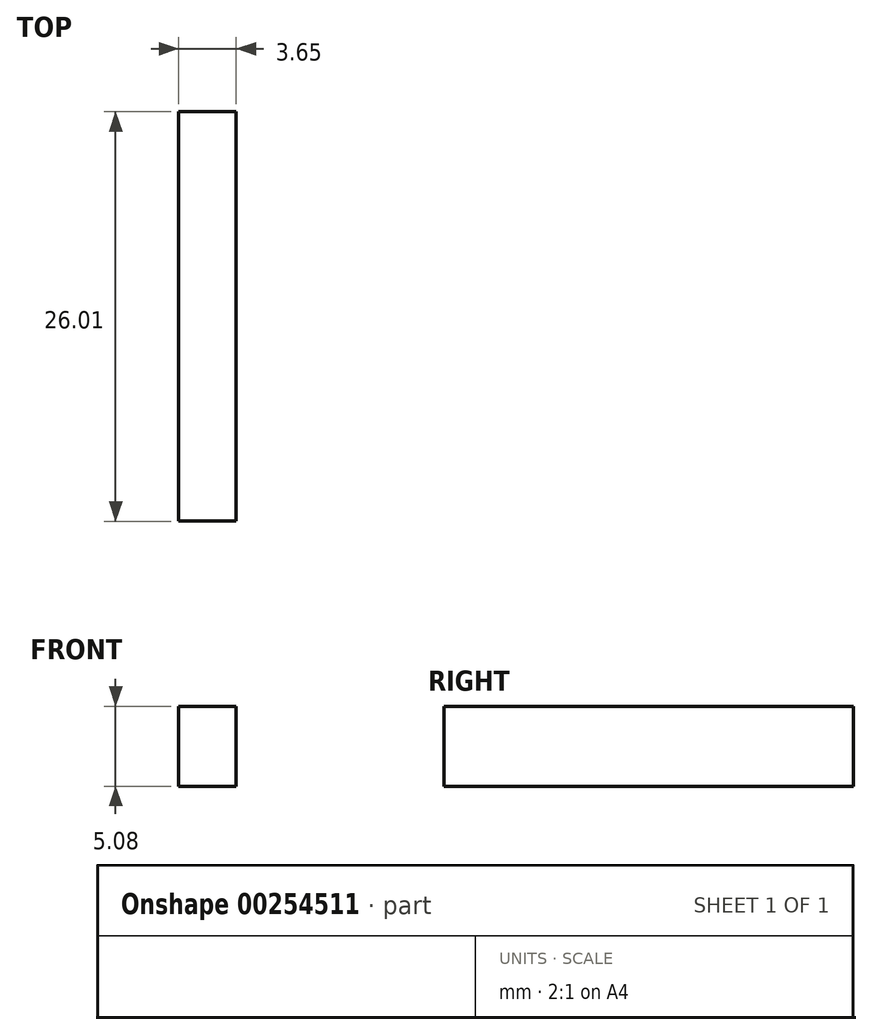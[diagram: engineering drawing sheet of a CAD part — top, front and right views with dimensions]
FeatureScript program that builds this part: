
annotation { "Feature Type Name" : "Feature", "Feature Type Description" : "" }
export const myFeature = defineFeature(function(context is Context, id is Id, definition is map)
    precondition{}
    {
        {
            var Q0;
            Q0=qCreatedBy(makeId("Top.planeOp"),FACE);
            var sketch = newSketch(context, id + "F0", { "sketchPlane" : qUnion([Q0])});
            skLineSegment(sketch, "E0", {"start": v(-33.45, 9.2) * mm, "end": v(-26.8, 16.12) * mm});
            skLineSegment(sketch, "E1", {"start": v(-26.8, 16.12) * mm, "end": v(-22.17, 16.12) * mm});
            skLineSegment(sketch, "E2", {"start": v(-22.17, 16.12) * mm, "end": v(-22.17, 19.99) * mm});
            skLineSegment(sketch, "E3", {"start": v(-22.17, 19.99) * mm, "end": v(-25.8, 19.97) * mm});
            skLineSegment(sketch, "E4", {"start": v(-25.8, 19.97) * mm, "end": v(-25.8, 38.73) * mm});
            skLineSegment(sketch, "E5", {"start": v(-25.8, 38.73) * mm, "end": v(-18.88, 45.9) * mm});
            skLineSegment(sketch, "E6", {"start": v(-18.88, 45.9) * mm, "end": v(14.3, 45.9) * mm});
            skLineSegment(sketch, "E7", {"start": v(14.3, 45.9) * mm, "end": v(22.2, 38.73) * mm});
            skLineSegment(sketch, "E8", {"start": v(22.2, 38.73) * mm, "end": v(22.2, 19.97) * mm});
            skLineSegment(sketch, "E9", {"start": v(22.2, 19.97) * mm, "end": v(18.52, 19.97) * mm});
            skLineSegment(sketch, "E10", {"start": v(18.52, 19.97) * mm, "end": v(18.52, 16.12) * mm});
            skLineSegment(sketch, "E11", {"start": v(18.52, 16.12) * mm, "end": v(22.2, 16.12) * mm});
            skLineSegment(sketch, "E12", {"start": v(22.2, 16.12) * mm, "end": v(29.83, 9.43) * mm});
            skLineSegment(sketch, "E13", {"start": v(29.83, 9.43) * mm, "end": v(29.83, -20.85) * mm});
            skLineSegment(sketch, "E14", {"start": v(29.83, -20.85) * mm, "end": v(22.14, -20.85) * mm});
            skLineSegment(sketch, "E15", {"start": v(22.14, -20.85) * mm, "end": v(22.14, -32.04) * mm});
            skLineSegment(sketch, "E16", {"start": v(22.14, -32.04) * mm, "end": v(19.03, -35.7) * mm});
            skLineSegment(sketch, "E17", {"start": v(19.03, -35.7) * mm, "end": v(3.87, -35.7) * mm});
            skLineSegment(sketch, "E18", {"start": v(3.87, -35.7) * mm, "end": v(3.87, -28.47) * mm});
            skLineSegment(sketch, "E19", {"start": v(3.87, -28.47) * mm, "end": v(-7.29, -28.47) * mm});
            skLineSegment(sketch, "E20", {"start": v(-7.29, -28.47) * mm, "end": v(-7.29, -35.7) * mm});
            skLineSegment(sketch, "E21", {"start": v(-7.29, -35.7) * mm, "end": v(-23.05, -35.7) * mm});
            skLineSegment(sketch, "E22", {"start": v(-23.05, -35.7) * mm, "end": v(-25.8, -32.44) * mm});
            skLineSegment(sketch, "E23", {"start": v(-25.8, -32.44) * mm, "end": v(-25.8, -20.85) * mm});
            skLineSegment(sketch, "E24", {"start": v(-25.8, -20.85) * mm, "end": v(-33.32, -20.85) * mm});
            skLineSegment(sketch, "E25", {"start": v(-33.32, -20.85) * mm, "end": v(-33.45, 9.2) * mm});
            skCircle(sketch, "E26", {"center": v(-11.3, 31.23) * mm, "radius": 5.9 * mm});
            skPoint(sketch, "E26.first.point", {"position": v(-17.19, 30.94) * mm});
            skPoint(sketch, "E26.second.point", {"position": v(-5.4, 31.07) * mm});
            skPoint(sketch, "E26.third.point", {"position": v(-11.26, 25.33) * mm});
            skCircle(sketch, "E27", {"center": v(7.12, 31) * mm, "radius": 5.64 * mm});
            skPoint(sketch, "E27.first.point", {"position": v(1.48, 30.84) * mm});
            skPoint(sketch, "E27.second.point", {"position": v(12.76, 30.78) * mm});
            skPoint(sketch, "E27.third.point", {"position": v(7.1, 36.64) * mm});
            skLineSegment(sketch, "E28.bottom", {"start": v(-14.96, 34.57) * mm, "end": v(-7.5, 34.57) * mm});
            skLineSegment(sketch, "E28.top", {"start": v(-14.96, 27.44) * mm, "end": v(-7.5, 27.44) * mm});
            skLineSegment(sketch, "E28.left", {"start": v(-14.96, 34.57) * mm, "end": v(-14.96, 27.44) * mm});
            skLineSegment(sketch, "E28.right", {"start": v(-7.5, 34.57) * mm, "end": v(-7.5, 27.44) * mm});
            skLineSegment(sketch, "E29.bottom", {"start": v(3.8, 34.28) * mm, "end": v(10.72, 34.28) * mm});
            skLineSegment(sketch, "E29.top", {"start": v(3.8, 27.44) * mm, "end": v(10.72, 27.44) * mm});
            skLineSegment(sketch, "E29.left", {"start": v(3.8, 34.28) * mm, "end": v(3.8, 27.44) * mm});
            skLineSegment(sketch, "E29.right", {"start": v(10.72, 34.28) * mm, "end": v(10.72, 27.44) * mm});
            skLineSegment(sketch, "E30.bottom", {"start": v(7.12, 31) * mm, "end": v(3.8, 31) * mm});
            skLineSegment(sketch, "E30.top", {"start": v(7.12, 34.28) * mm, "end": v(3.8, 34.28) * mm});
            skLineSegment(sketch, "E30.left", {"start": v(7.12, 31) * mm, "end": v(7.12, 34.28) * mm});
            skLineSegment(sketch, "E30.right", {"start": v(3.8, 31) * mm, "end": v(3.8, 34.28) * mm});
            skLineSegment(sketch, "E31.bottom", {"start": v(-11.3, 31.23) * mm, "end": v(-14.96, 31.23) * mm});
            skLineSegment(sketch, "E31.top", {"start": v(-11.3, 34.57) * mm, "end": v(-14.96, 34.57) * mm});
            skLineSegment(sketch, "E31.left", {"start": v(-11.3, 31.23) * mm, "end": v(-11.3, 34.57) * mm});
            skLineSegment(sketch, "E31.right", {"start": v(-14.96, 31.23) * mm, "end": v(-14.96, 34.57) * mm});
            skLineSegment(sketch, "E32.bottom", {"start": v(-3.8, 23.6) * mm, "end": v(0, 23.6) * mm});
            skLineSegment(sketch, "E32.top", {"start": v(-3.8, 19.8) * mm, "end": v(0, 19.8) * mm});
            skLineSegment(sketch, "E32.left", {"start": v(-3.8, 23.6) * mm, "end": v(-3.8, 19.8) * mm});
            skLineSegment(sketch, "E32.right", {"start": v(0, 23.6) * mm, "end": v(0, 19.8) * mm});
            skLineSegment(sketch, "E33.bottom", {"start": v(-7.5, 15.86) * mm, "end": v(3.8, 15.86) * mm});
            skLineSegment(sketch, "E33.top", {"start": v(-7.5, 12.27) * mm, "end": v(3.8, 12.27) * mm});
            skLineSegment(sketch, "E33.left", {"start": v(-7.5, 15.86) * mm, "end": v(-7.5, 12.27) * mm});
            skLineSegment(sketch, "E33.right", {"start": v(3.8, 15.86) * mm, "end": v(3.8, 12.27) * mm});
            skPoint(sketch, "E34.oppositeSnap0", {"position": v(-25.8, -26.64) * mm});
            skLineSegment(sketch, "E34.bottom", {"start": v(-29.45, -9.9) * mm, "end": v(-25.8, -9.9) * mm});
            skLineSegment(sketch, "E34.top", {"start": v(-29.45, -17.27) * mm, "end": v(-25.8, -17.27) * mm});
            skLineSegment(sketch, "E34.left", {"start": v(-29.45, -9.9) * mm, "end": v(-29.45, -17.27) * mm});
            skLineSegment(sketch, "E34.right", {"start": v(-25.8, -9.9) * mm, "end": v(-25.8, -17.27) * mm});
            skLineSegment(sketch, "E35.top", {"start": v(-29.45, 8.74) * mm, "end": v(-25.8, 8.74) * mm});
            skLineSegment(sketch, "E35.left", {"start": v(-29.45, -9.9) * mm, "end": v(-29.45, 8.74) * mm});
            skLineSegment(sketch, "E35.right", {"start": v(-25.8, -9.9) * mm, "end": v(-25.8, 8.74) * mm});
            skLineSegment(sketch, "E36.bottom", {"start": v(22.2, -9.9) * mm, "end": v(25.76, -9.9) * mm});
            skLineSegment(sketch, "E36.top", {"start": v(22.2, -17.27) * mm, "end": v(25.76, -17.27) * mm});
            skLineSegment(sketch, "E36.left", {"start": v(22.2, -9.9) * mm, "end": v(22.2, -17.27) * mm});
            skLineSegment(sketch, "E36.right", {"start": v(25.76, -9.9) * mm, "end": v(25.76, -17.27) * mm});
            skLineSegment(sketch, "E37.top", {"start": v(22.2, 8.7) * mm, "end": v(25.76, 8.7) * mm});
            skLineSegment(sketch, "E37.left", {"start": v(22.2, -9.9) * mm, "end": v(22.2, 8.7) * mm});
            skLineSegment(sketch, "E37.right", {"start": v(25.76, -9.9) * mm, "end": v(25.76, 8.7) * mm});
            skLineSegment(sketch, "E38.bottom", {"start": v(-3.6, -28.47) * mm, "end": v(0, -28.47) * mm});
            skLineSegment(sketch, "E38.top", {"start": v(-3.6, -24.74) * mm, "end": v(0, -24.74) * mm});
            skLineSegment(sketch, "E38.left", {"start": v(-3.6, -28.47) * mm, "end": v(-3.6, -24.74) * mm});
            skLineSegment(sketch, "E38.right", {"start": v(0, -28.47) * mm, "end": v(0, -24.74) * mm});
            skLineSegment(sketch, "E39", {"start": v(-22.24, -24.61) * mm, "end": v(-22.24, -31.85) * mm});
            skLineSegment(sketch, "E40", {"start": v(-22.24, -31.85) * mm, "end": v(-11.06, -31.85) * mm});
            skLineSegment(sketch, "E41", {"start": v(-11.06, -31.85) * mm, "end": v(-11.06, -28.48) * mm});
            skLineSegment(sketch, "E42", {"start": v(-11.06, -28.48) * mm, "end": v(-7.29, -28.47) * mm});
            skLineSegment(sketch, "E43", {"start": v(-7.29, -24.61) * mm, "end": v(-22.24, -24.61) * mm});
            skLineSegment(sketch, "E44", {"start": v(-7.29, -24.61) * mm, "end": v(-7.29, -28.47) * mm});
            skLineSegment(sketch, "E45", {"start": v(3.87, -28.47) * mm, "end": v(3.87, -24.61) * mm});
            skLineSegment(sketch, "E46", {"start": v(3.87, -24.61) * mm, "end": v(18.56, -24.61) * mm});
            skLineSegment(sketch, "E47", {"start": v(18.56, -24.61) * mm, "end": v(18.56, -31.97) * mm});
            skLineSegment(sketch, "E48", {"start": v(18.56, -31.97) * mm, "end": v(7.4, -31.97) * mm});
            skLineSegment(sketch, "E49", {"start": v(7.4, -31.97) * mm, "end": v(7.4, -28.47) * mm});
            skLineSegment(sketch, "E50", {"start": v(7.4, -28.47) * mm, "end": v(3.87, -28.47) * mm});
            skLineSegment(sketch, "E51", {"start": v(-22.17, 19.99) * mm, "end": v(-22.24, 38.23) * mm});
            skLineSegment(sketch, "E52", {"start": v(-22.24, 38.23) * mm, "end": v(-18.48, 38.25) * mm});
            skLineSegment(sketch, "E53", {"start": v(-18.48, 38.25) * mm, "end": v(-18.5, 42.04) * mm});
            skLineSegment(sketch, "E54", {"start": v(-18.5, 42.04) * mm, "end": v(14.76, 42.16) * mm});
            skLineSegment(sketch, "E55", {"start": v(14.76, 42.16) * mm, "end": v(14.78, 38.23) * mm});
            skLineSegment(sketch, "E56", {"start": v(14.78, 38.23) * mm, "end": v(18.52, 38.24) * mm});
            skLineSegment(sketch, "E57", {"start": v(18.52, 38.24) * mm, "end": v(18.52, 19.97) * mm});
            skLineSegment(sketch, "E58", {"start": v(3.8, 15.86) * mm, "end": v(3.8, 19.97) * mm});
            skLineSegment(sketch, "E59", {"start": v(3.8, 19.97) * mm, "end": v(18.52, 19.97) * mm});
            skLineSegment(sketch, "E60", {"start": v(-7.5, 15.86) * mm, "end": v(-7.5, 19.99) * mm});
            skLineSegment(sketch, "E61", {"start": v(-7.5, 19.99) * mm, "end": v(-22.17, 19.99) * mm});
            skLineSegment(sketch, "E62", {"start": v(-22.23, 12.38) * mm, "end": v(-22.23, -21.38) * mm});
            skLineSegment(sketch, "E63", {"start": v(-22.23, -21.38) * mm, "end": v(18.48, -21.38) * mm});
            skLineSegment(sketch, "E64", {"start": v(18.48, -21.38) * mm, "end": v(18.48, 12.34) * mm});
            skLineSegment(sketch, "E65", {"start": v(18.48, 12.34) * mm, "end": v(14.65, 12.34) * mm});
            skLineSegment(sketch, "E66", {"start": v(14.65, 12.34) * mm, "end": v(14.65, 15.86) * mm});
            skLineSegment(sketch, "E67", {"start": v(14.65, 15.86) * mm, "end": v(3.8, 15.86) * mm});
            skLineSegment(sketch, "E68", {"start": v(-22.23, 12.38) * mm, "end": v(-18.53, 12.38) * mm});
            skLineSegment(sketch, "E69", {"start": v(-18.53, 12.38) * mm, "end": v(-18.53, 15.86) * mm});
            skLineSegment(sketch, "E70", {"start": v(-18.53, 15.86) * mm, "end": v(-7.5, 15.86) * mm});
            skLineSegment(sketch, "E71.bottom", {"start": v(-7.42, -28.31) * mm, "end": v(-7.13, -28.31) * mm});
            skLineSegment(sketch, "E71.top", {"start": v(-7.42, -28.63) * mm, "end": v(-7.13, -28.63) * mm});
            skLineSegment(sketch, "E71.left", {"start": v(-7.42, -28.31) * mm, "end": v(-7.42, -28.63) * mm});
            skLineSegment(sketch, "E71.right", {"start": v(-7.13, -28.31) * mm, "end": v(-7.13, -28.63) * mm});
            skLineSegment(sketch, "E72.bottom", {"start": v(3.95, -28.38) * mm, "end": v(3.78, -28.38) * mm});
            skLineSegment(sketch, "E72.top", {"start": v(3.95, -28.56) * mm, "end": v(3.78, -28.56) * mm});
            skLineSegment(sketch, "E72.left", {"start": v(3.95, -28.38) * mm, "end": v(3.95, -28.56) * mm});
            skLineSegment(sketch, "E72.right", {"start": v(3.78, -28.38) * mm, "end": v(3.78, -28.56) * mm});
            skSolve(sketch);
        }
        {
            var Q0;
            Q0=makeQuery(id+"F0.imprint","IMPRINT",FACE,{"disambiguationData":[TD([[makeQuery(id+"F0.imprint","IMPRINT",EDGE,{"derivedFrom":sQuery(id+"F0.wireOp",EDGE,"E34.bottom")}),1.0]])]});
            var Q1;
            Q1=makeQuery(id+"F0.imprint","IMPRINT",FACE,{"disambiguationData":[TD([[makeQuery(id+"F0.imprint","IMPRINT",EDGE,{"derivedFrom":sQuery(id+"F0.wireOp",EDGE,"E34.top")}),1.0]])]});
            extrude(context, id + "F1", {"entities" : qUnion([Q0, Q1]), "depth" : 5.08 * mm});
        }
    });
